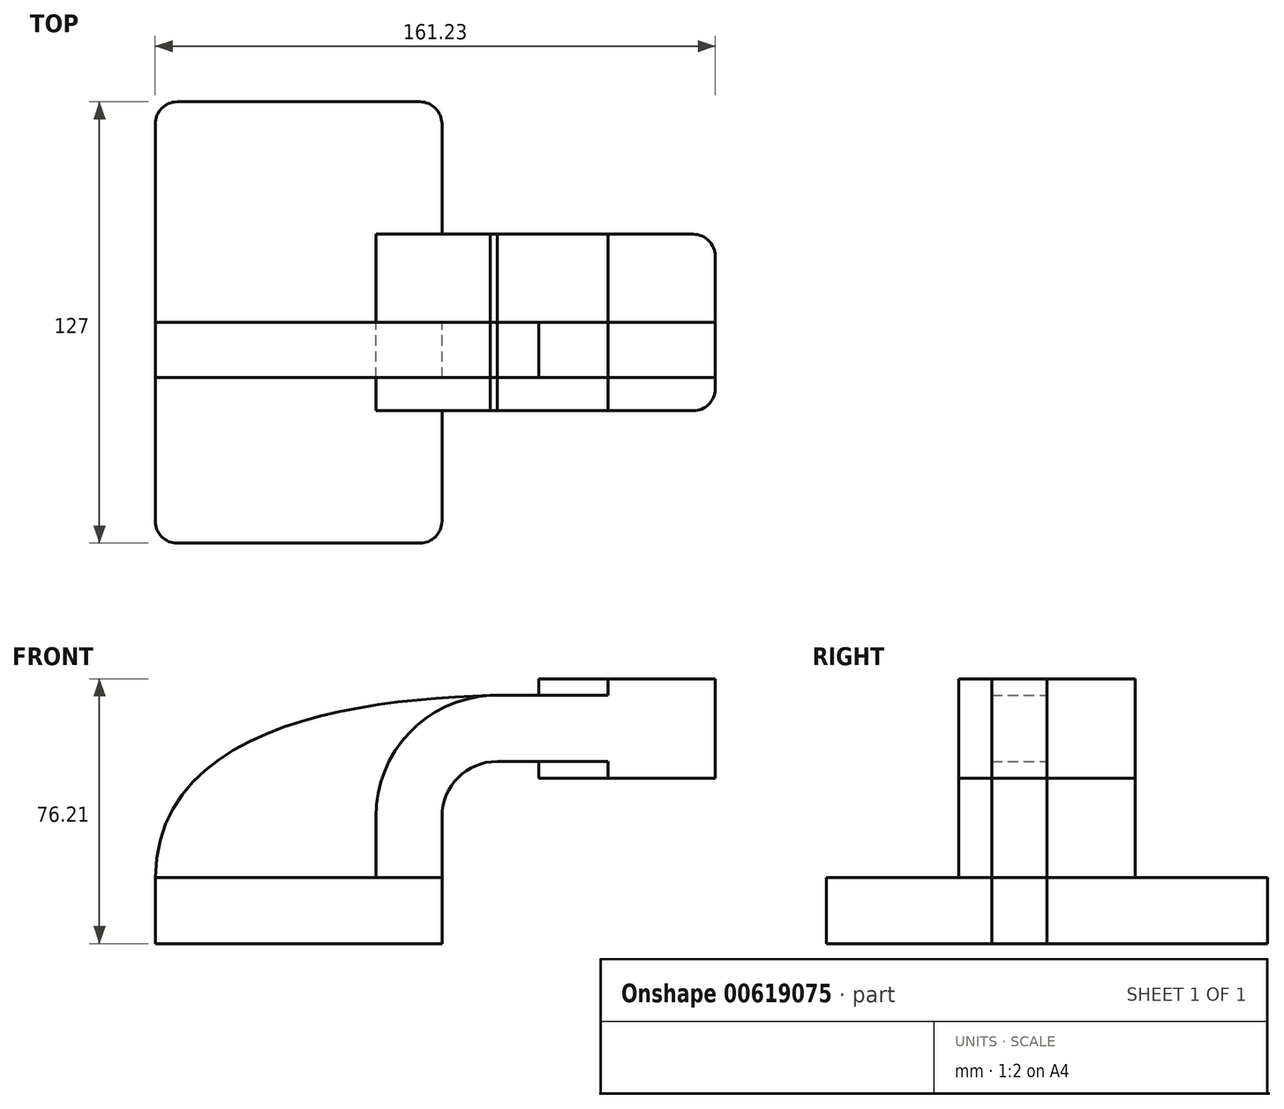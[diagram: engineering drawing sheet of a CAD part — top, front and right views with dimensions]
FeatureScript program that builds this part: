
annotation { "Feature Type Name" : "Feature", "Feature Type Description" : "" }
export const myFeature = defineFeature(function(context is Context, id is Id, definition is map)
    precondition{}
    {
        {
            var Q0;
            Q0=qCreatedBy(makeId("Front.planeOp"),FACE);
            var sketch = newSketch(context, id + "F0", { "sketchPlane" : qUnion([Q0])});
            skLineSegment(sketch, "E0.bottom", {"start": v(-41.28, 9.52) * mm, "end": v(41.27, 9.53) * mm});
            skLineSegment(sketch, "E0.top", {"start": v(-41.28, -9.53) * mm, "end": v(41.28, -9.53) * mm});
            skLineSegment(sketch, "E0.left", {"start": v(-41.28, 9.52) * mm, "end": v(-41.27, -9.53) * mm});
            skLineSegment(sketch, "E0.right", {"start": v(41.28, 9.53) * mm, "end": v(41.28, -9.52) * mm});
            skPoint(sketch, "E0.middle", {"position": v(0, 0) * mm});
            skLineSegment(sketch, "E1", {"start": v(41.27, 9.53) * mm, "end": v(41.27, 27) * mm});
            skLineSegment(sketch, "E2.bottom", {"start": v(69.15, 66.67) * mm, "end": v(119.95, 66.67) * mm});
            skLineSegment(sketch, "E2.top", {"start": v(69.15, 38.1) * mm, "end": v(119.95, 38.1) * mm});
            skLineSegment(sketch, "E2.left", {"start": v(69.15, 66.67) * mm, "end": v(69.15, 38.1) * mm});
            skLineSegment(sketch, "E2.right", {"start": v(119.95, 66.67) * mm, "end": v(119.95, 38.1) * mm});
            skPoint(sketch, "E2.middle", {"position": v(94.55, 52.39) * mm});
            skLineSegment(sketch, "E3", {"start": v(41.27, 27) * mm, "end": v(41.27, 27) * mm});
            skArc(sketch, "E4", {"start": v(41.27, 27) * mm, "mid": v(45.92, 38.23) * mm, "end": v(57.15, 42.88) * mm});
            skLineSegment(sketch, "E5", {"start": v(57.15, 42.88) * mm, "end": v(89.1, 42.88) * mm});
            skLineSegment(sketch, "E6.0", {"start": v(57.15, 61.93) * mm, "end": v(89.1, 61.93) * mm});
            skArc(sketch, "E6.1", {"start": v(22.22, 27) * mm, "mid": v(32.45, 51.7) * mm, "end": v(57.15, 61.93) * mm});
            skLineSegment(sketch, "E6.2", {"start": v(22.22, 9.53) * mm, "end": v(22.22, 27) * mm});
            skLineSegment(sketch, "E7", {"start": v(89.1, 42.88) * mm, "end": v(89.1, 61.93) * mm});
            skLineSegment(sketch, "E8", {"start": v(89.1, 42.88) * mm, "end": v(89.1, 38.1) * mm});
            skLineSegment(sketch, "E9", {"start": v(89.1, 38.1) * mm, "end": v(89.1, 66.67) * mm});
            skFitSpline(sketch, "E10", {"points": [v(-41.28, 9.52) * mm, v(57.15, 61.93) * mm], "startDerivative": vector(2.3, 134.33) * mm, "endDerivative": vector(112.77, 2.85) * mm});
            skSolve(sketch);
        }
        {
            var Q0;
            Q0=makeQuery(id+"F0.imprint","IMPRINT",FACE,{"disambiguationData":[TD([[makeQuery(id+"F0.imprint","IMPRINT",EDGE,{"derivedFrom":sQuery(id+"F0.wireOp",EDGE,"E0.top")}),1.0]])]});
            extrude(context, id + "F1", {"entities" : qUnion([Q0]), "endBound" : BoundingType.SYMMETRIC, "depth" : 127 * mm, "offsetDistance" : 25.4 * mm});
        }
        {
            var Q0;
            {var subQ1=sQuery(id+"F0.wireOp",EDGE,"E1");Q0=makeQuery(id+"F0.imprint","IMPRINT",FACE,{"disambiguationData":[TD([[makeQuery(id+"F0.imprint","IMPRINT",EDGE,{"derivedFrom":subQ1}),1.0]])]});}
            var Q1;
            {var subQ0=sQuery(id+"F0.wireOp",EDGE,"E2.right");Q1=makeQuery(id+"F0.imprint","IMPRINT",FACE,{"disambiguationData":[TD([[makeQuery(id+"F0.imprint","IMPRINT",EDGE,{"derivedFrom":subQ0}),-1.0]])]});}
            var Q2;
            {var subQ0=sQuery(id+"F0.wireOp",EDGE,"E6.0");var subQ1=sQuery(id+"F0.wireOp",EDGE,"E2.left");var subQ2=makeQuery(id+"F0.imprint","INTERSECT",VERTEX,{"derivedFrom":[subQ1,subQ0]});Q2=makeQuery(id+"F0.imprint","IMPRINT",FACE,{"disambiguationData":[TD([[makeQuery(id+"F0.imprint","IMPRINT",EDGE,{"disambiguationData":[TD([[subQ2,-1.0]])],"derivedFrom":subQ1}),1.0]])]});}
            extrude(context, id + "F2", {"entities" : qUnion([Q0, Q1, Q2]), "endBound" : BoundingType.SYMMETRIC, "depth" : 50.8 * mm, "offsetDistance" : 25.4 * mm});
        }
        {
            var Q0;
            Q0 = qSketchRegion(id + "F0", true);
            extrude(context, id + "F3", {"entities" : qUnion([Q0]), "depth" : 15.88 * mm, "offsetDistance" : 25.4 * mm});
        }
        {
            var Q0;
            Q0=makeQuery(id+"F1.opExtrude","CAP_EDGE",EDGE,{"disambiguationData":[OSD([sQuery(id+"F0.wireOp",EDGE,"E0.right")])],"isStart":false});
            var Q1;
            Q1=makeQuery(id+"F1.opExtrude","CAP_EDGE",EDGE,{"disambiguationData":[OSD([sQuery(id+"F0.wireOp",EDGE,"E0.left")])],"isStart":false});
            fillet(context, id + "F4", {"entities" : qUnion([Q0, Q1]), "radius" : 6.35 * mm, "tangentPropagation" : true, "allowEdgeOverflow" : false});
        }
        {
            var Q0;
            Q0=makeQuery(id+"F1.opExtrude","CAP_EDGE",EDGE,{"disambiguationData":[OSD([sQuery(id+"F0.wireOp",EDGE,"E0.left")])],"isStart":true});
            var Q1;
            Q1=makeQuery(id+"F1.opExtrude","CAP_EDGE",EDGE,{"disambiguationData":[OSD([sQuery(id+"F0.wireOp",EDGE,"E0.right")])],"isStart":true});
            var Q2;
            Q2=makeQuery(id+"F2.opExtrude","CAP_EDGE",EDGE,{"disambiguationData":[OSD([sQuery(id+"F0.wireOp",EDGE,"E2.right")])],"isStart":true});
            var Q3;
            Q3=makeQuery(id+"F2.opExtrude","CAP_EDGE",EDGE,{"disambiguationData":[OSD([sQuery(id+"F0.wireOp",EDGE,"E2.right")])],"isStart":false});
            fillet(context, id + "F5", {"entities" : qUnion([Q0, Q1, Q2, Q3]), "radius" : 6.35 * mm, "tangentPropagation" : true, "allowEdgeOverflow" : false});
        }
    });
